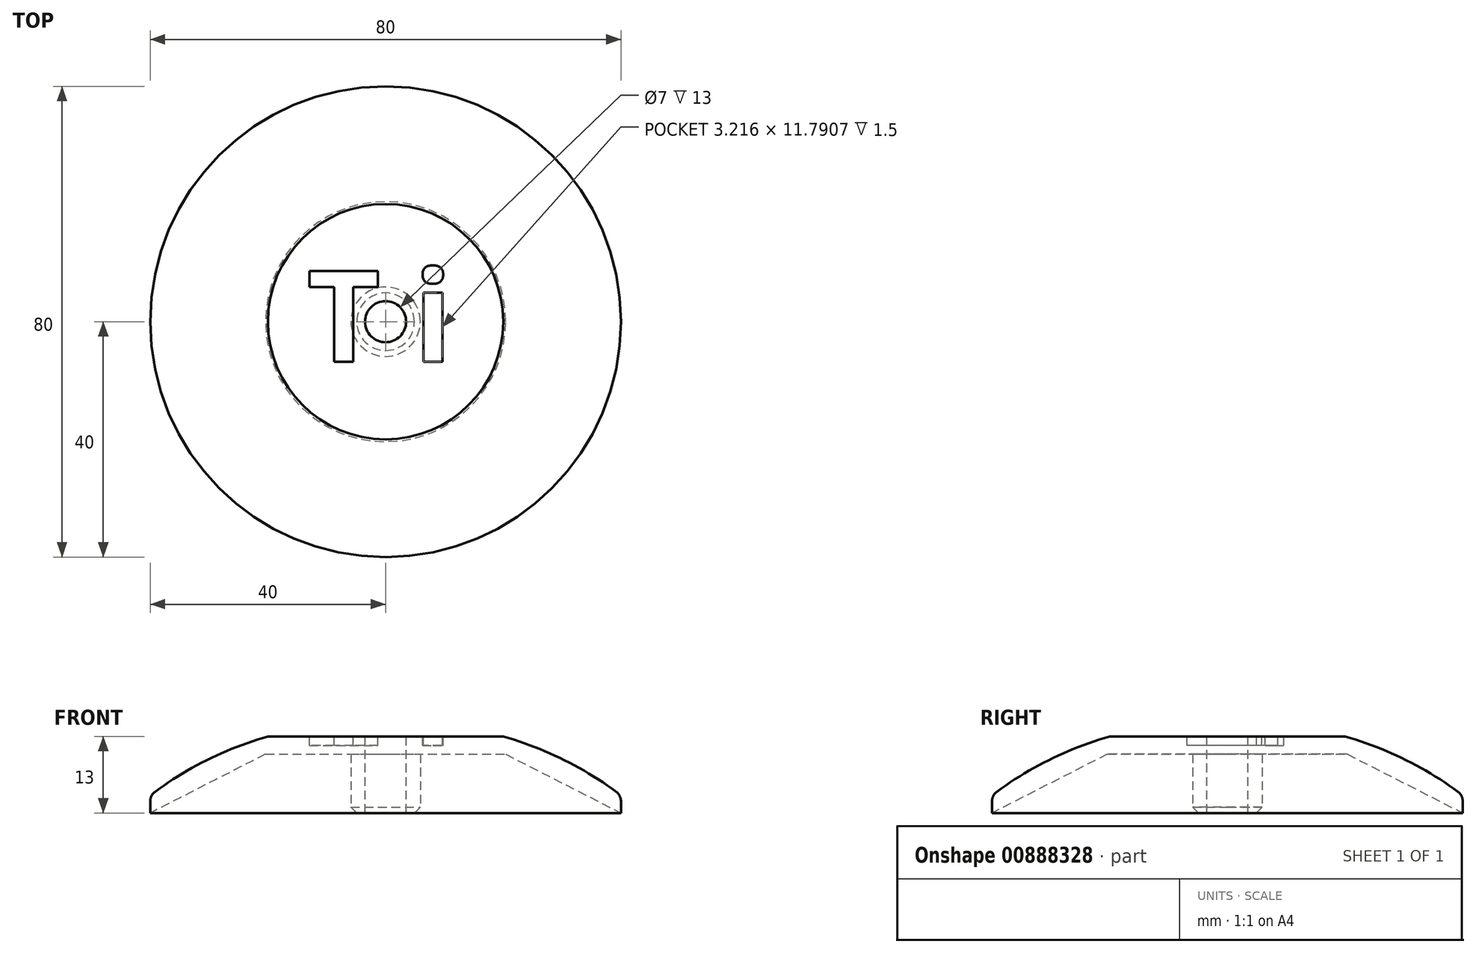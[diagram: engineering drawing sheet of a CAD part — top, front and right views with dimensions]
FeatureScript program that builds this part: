
annotation { "Feature Type Name" : "Feature", "Feature Type Description" : "" }
export const myFeature = defineFeature(function(context is Context, id is Id, definition is map)
    precondition{}
    {
        {
            var Q0;
            Q0=qCreatedBy(makeId("Front.planeOp"),FACE);
            var sketch = newSketch(context, id + "F0", { "sketchPlane" : qUnion([Q0])});
            skLineSegment(sketch, "E0", {"start": v(0, 0) * mm, "end": v(-5.9, 0) * mm});
            skLineSegment(sketch, "E1", {"start": v(-5.9, 0) * mm, "end": v(-5.9, 10) * mm});
            skLineSegment(sketch, "E2", {"start": v(-5.9, 10) * mm, "end": v(-20.4, 10) * mm});
            skLineSegment(sketch, "E3", {"start": v(-20.4, 10) * mm, "end": v(-40, 0) * mm});
            skLineSegment(sketch, "E4", {"start": v(-40, 0) * mm, "end": v(-40, 3) * mm});
            skLineSegment(sketch, "E5", {"start": v(0, 0) * mm, "end": v(0, 13) * mm});
            skLineSegment(sketch, "E6", {"start": v(0, 13) * mm, "end": v(-20, 13) * mm});
            skArc(sketch, "E7", {"start": v(-20, 13) * mm, "mid": v(-30.47, 8.94) * mm, "end": v(-40, 3) * mm});
            skSolve(sketch);
        }
        {
            var Q0;
            Q0=makeQuery(id+"F0.imprint","IMPRINT",FACE,{"disambiguationData":[TD([[makeQuery(id+"F0.imprint","IMPRINT",EDGE,{"derivedFrom":sQuery(id+"F0.wireOp",EDGE,"E0")}),-1.0]])]});
            var Q1;
            Q1=sQuery(id+"F0.wireOp",EDGE,"E5");
            revolve(context, id + "F1", {"surfaceOperationType" : NewSurfaceOperationType.NEW, "entities" : qUnion([Q0]), "axis" : qUnion([Q1]), "revolveType" : RevolveType.FULL});
        }
        {
            var Q0;
            Q0=makeQuery(id+"F1.opRevolve","SWEPT_FACE",FACE,{"disambiguationData":[OSD([sQuery(id+"F0.wireOp",EDGE,"E6")])]});
            var sketch = newSketch(context, id + "F2", { "sketchPlane" : qUnion([Q0])});
            skText(sketch, "E8", { "text": "T i", "fontName": "OpenSans-Bold.ttf"});
            const initialGuessF2  = {"E8": [-0.01338, -0.00683, 1, 0, 0.01555]};
            skSetInitialGuess(sketch, initialGuessF2);
            skSolve(sketch);
        }
        {
            var Q0;
            Q0=qSketchRegion(id+"F2",true);
            extrude(context, id + "F3", {"entities" : qUnion([Q0]), "operationType" : NewBodyOperationType.REMOVE, "oppositeDirection" : true, "depth" : 1.5 * mm, "offsetDistance" : 25 * mm});
        }
        {
            var Q0;
            Q0=makeQuery(id+"F1.opRevolve","SWEPT_EDGE",EDGE,{"disambiguationData":[OSD([sQuery(id+"F0.wireOp",EDGE,"E0"),sQuery(id+"F0.wireOp",EDGE,"E1")])]});
            chamfer(context, id + "F4", {"entities" : qUnion([Q0]), "width" : 1 * mm, "tangentPropagation" : true});
        }
        {
            var Q0;
            Q0=makeQuery(id+"F1.opRevolve","SWEPT_FACE",FACE,{"disambiguationData":[OSD([sQuery(id+"F0.wireOp",EDGE,"E6")])]});
            var sketch = newSketch(context, id + "F5", { "sketchPlane" : qUnion([Q0])});
            skCircle(sketch, "E9", {"center": v(0, 0) * mm, "radius": 3.5 * mm});
            skSolve(sketch);
        }
        {
            var Q0;
            Q0=makeQuery(id+"F5.imprint","IMPRINT",FACE,{"disambiguationData":[TD([[makeQuery(id+"F5.imprint","IMPRINT",EDGE,{"derivedFrom":sQuery(id+"F5.wireOp",EDGE,"E9")}),1.0]])]});
            extrude(context, id + "F6", {"entities" : qUnion([Q0]), "operationType" : NewBodyOperationType.REMOVE, "endBound" : BoundingType.THROUGH_ALL, "oppositeDirection" : true, "depth" : 25 * mm, "offsetDistance" : 25 * mm});
        }
        {
            var Q0;
            Q0=makeQuery(id+"F1.opRevolve","SWEPT_EDGE",EDGE,{"disambiguationData":[OSD([sQuery(id+"F0.wireOp",EDGE,"E4"),sQuery(id+"F0.wireOp",EDGE,"E7")])]});
            fillet(context, id + "F7", {"entities" : qUnion([Q0]), "radius" : 2 * mm, "tangentPropagation" : true, "allowEdgeOverflow" : false});
        }
    });
